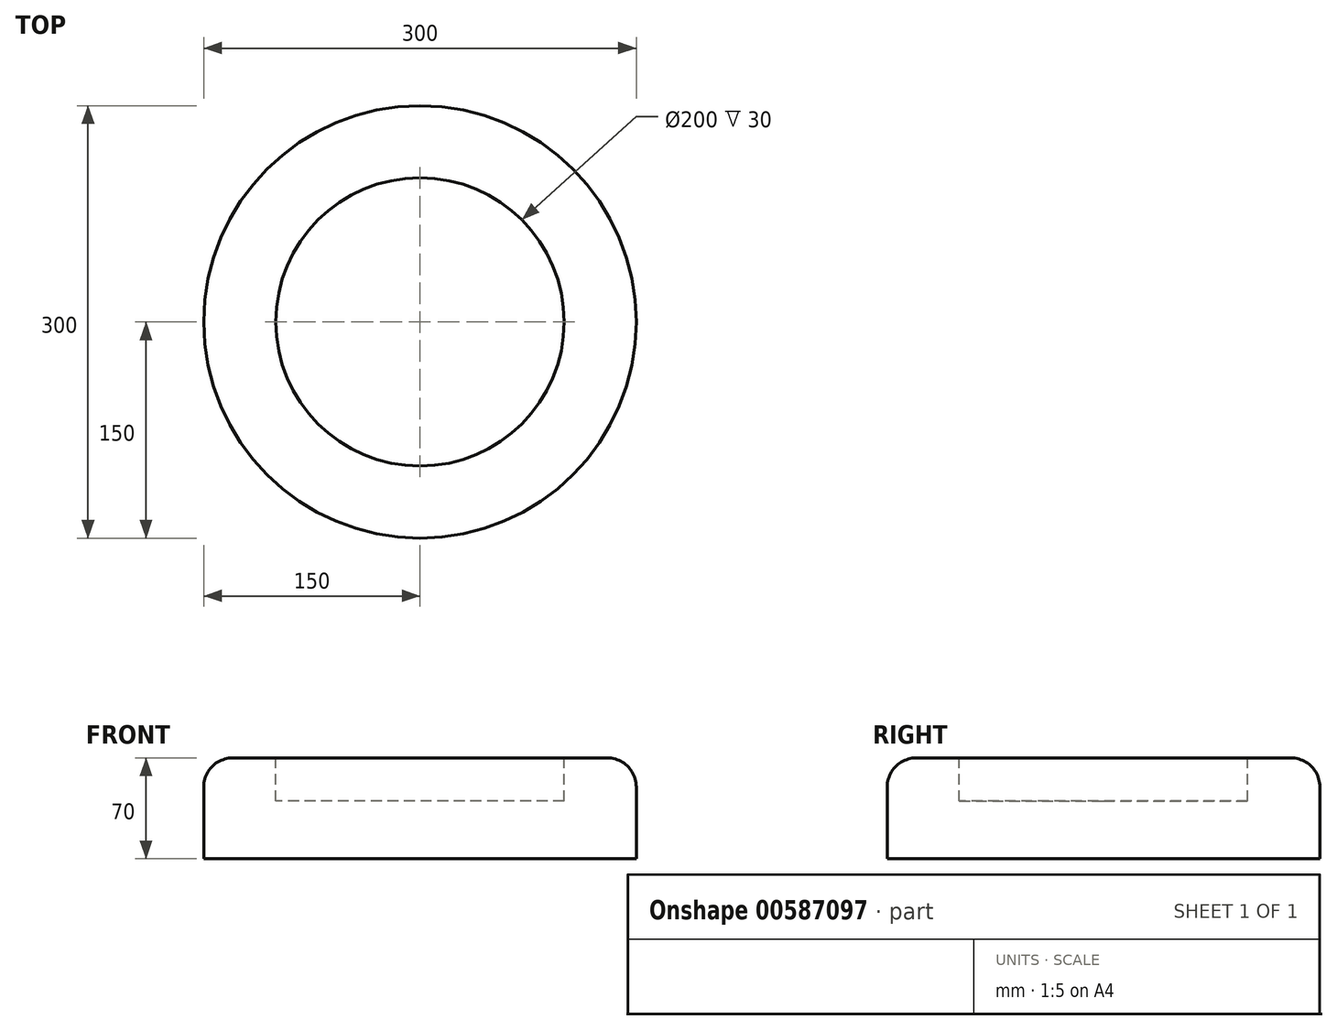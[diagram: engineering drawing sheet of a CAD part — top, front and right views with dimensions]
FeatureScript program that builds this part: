
annotation { "Feature Type Name" : "Feature", "Feature Type Description" : "" }
export const myFeature = defineFeature(function(context is Context, id is Id, definition is map)
    precondition{}
    {
        {
            var Q0;
            Q0=qCreatedBy(makeId("Front.planeOp"),FACE);
            var sketch = newSketch(context, id + "F0", { "sketchPlane" : qUnion([Q0])});
            skLineSegment(sketch, "E0", {"start": v(0, 0) * mm, "end": v(150, 0) * mm});
            skLineSegment(sketch, "E1", {"start": v(150, 0) * mm, "end": v(150, 70) * mm});
            skLineSegment(sketch, "E2", {"start": v(150, 70) * mm, "end": v(100, 70) * mm});
            skLineSegment(sketch, "E3", {"start": v(100, 70) * mm, "end": v(100, 40) * mm});
            skLineSegment(sketch, "E4", {"start": v(100, 40) * mm, "end": v(0, 40) * mm});
            skLineSegment(sketch, "E5", {"start": v(0, 40) * mm, "end": v(0, 0) * mm});
            skSolve(sketch);
        }
        {
            var Q0;
            Q0=makeQuery(id+"F0.imprint","IMPRINT",FACE,{"disambiguationData":[TD([[makeQuery(id+"F0.imprint","IMPRINT",EDGE,{"derivedFrom":sQuery(id+"F0.wireOp",EDGE,"E0")}),1.0]])]});
            var Q1;
            Q1=sQuery(id+"F0.wireOp",EDGE,"E5");
            revolve(context, id + "F1", {"entities" : qUnion([Q0]), "axis" : qUnion([Q1]), "revolveType" : RevolveType.FULL});
        }
        {
            var Q0;
            Q0=makeQuery(id+"F1.opRevolve","SWEPT_EDGE",EDGE,{"disambiguationData":[OSD([sQuery(id+"F0.wireOp",EDGE,"E1"),sQuery(id+"F0.wireOp",EDGE,"E2")])]});
            fillet(context, id + "F2", {"entities" : qUnion([Q0]), "radius" : 20 * mm, "tangentPropagation" : true, "allowEdgeOverflow" : false});
        }
        {
            var Q0;
            Q0=makeQuery(id+"F1.opRevolve","SWEPT_FACE",FACE,{"disambiguationData":[OSD([sQuery(id+"F0.wireOp",EDGE,"E0")])]});
            cPlane(context, id + "F3", {"entities" : qUnion([Q0]), "cplaneType" : CPlaneType.OFFSET, "offset" : 200 * mm, "width" : 150 * mm, "height" : 150 * mm});
        }
    });
